# Revit family: ITK_Телефонная патч-панель_19-дюймовое крепление_1U_категория 3
name_source: partatom
category: Обобщенные модели
units: mm (PartAtom-declared; Revit-internal decimal feet)

## family parameters
Всегда вертикально = Да
Может служить основой для арматурных стержней = Нет
На основе рабочей плоскости = Нет
Общий = Нет
При загрузке вырезать с полостями = Нет
Размер круглого соединителя = Использовать диаметр
Тип детали = Нормальный
Точка расчета площади = Нет

## types (1)
- PP25-1UC03U-110
    ADSK_URL страницы изделия = https://www.itk-group.ru
    ADSK_Версия Revit = 2019
    ADSK_Версия семейства = 1.0
    ADSK_Группирование = I. ЩИТЫ И ПУЛЬТЫ
    ADSK_Единица измерения = шт
    ADSK_Завод-изготовитель = IEK
    ADSK_Код изделия = PP25-1UC03U-110
    ADSK_Масса = 0.63
    ADSK_Материал наименование = Металл и АБС-пластик
    ADSK_Наименование = ITK 1U телефонная патч-панель категории 3 25 портов 110 IDC
    IEK_URL = https://www.itk-group.ru
    IEK_Описание = Компактное решение.
Двойная понятная маркировка IDC-модулей и портов.
Расширенный частотный диапазон работы.
Увеличенное количество циклов включения-отключения.
Совместимы со всеми 19" шкафами и стойками ITK.
Соответствие международным стандартам и ГОСТ Р.
    IEK_Цена за единицу = 1895.9
    KSI_CMa_Строительные материалы = 10.03.02.06
    KSI_CPr_Строительные изделия = 27.12.31.61.1.04.09-1090
    URL = https://www.iek.ru
    Высота = 45 мм
    Глубина = 23 мм
    Изготовитель = ITK
    Материал = Окраска - RAL 9005
    Ширина = 483 мм
